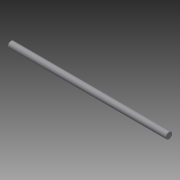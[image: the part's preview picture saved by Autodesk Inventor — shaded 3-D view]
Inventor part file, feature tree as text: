
AUTODESK INVENTOR PART (.ipt)
format: ipt  version: 2013 (Build 170138000, 138)  size: 63,488 bytes
history: native  units: mm
features: other x1, extrude x1, sketch x1
ambient origin geometry x8: Origin, YZ Plane, XZ Plane, XY Plane, X Axis, Y Axis, Z Axis, Center Point
feature tree (3):
  other  "ソリッド1"
  extrude  "押し出し1"  Depth=2.0mm
  sketch  "スケッチ1"
